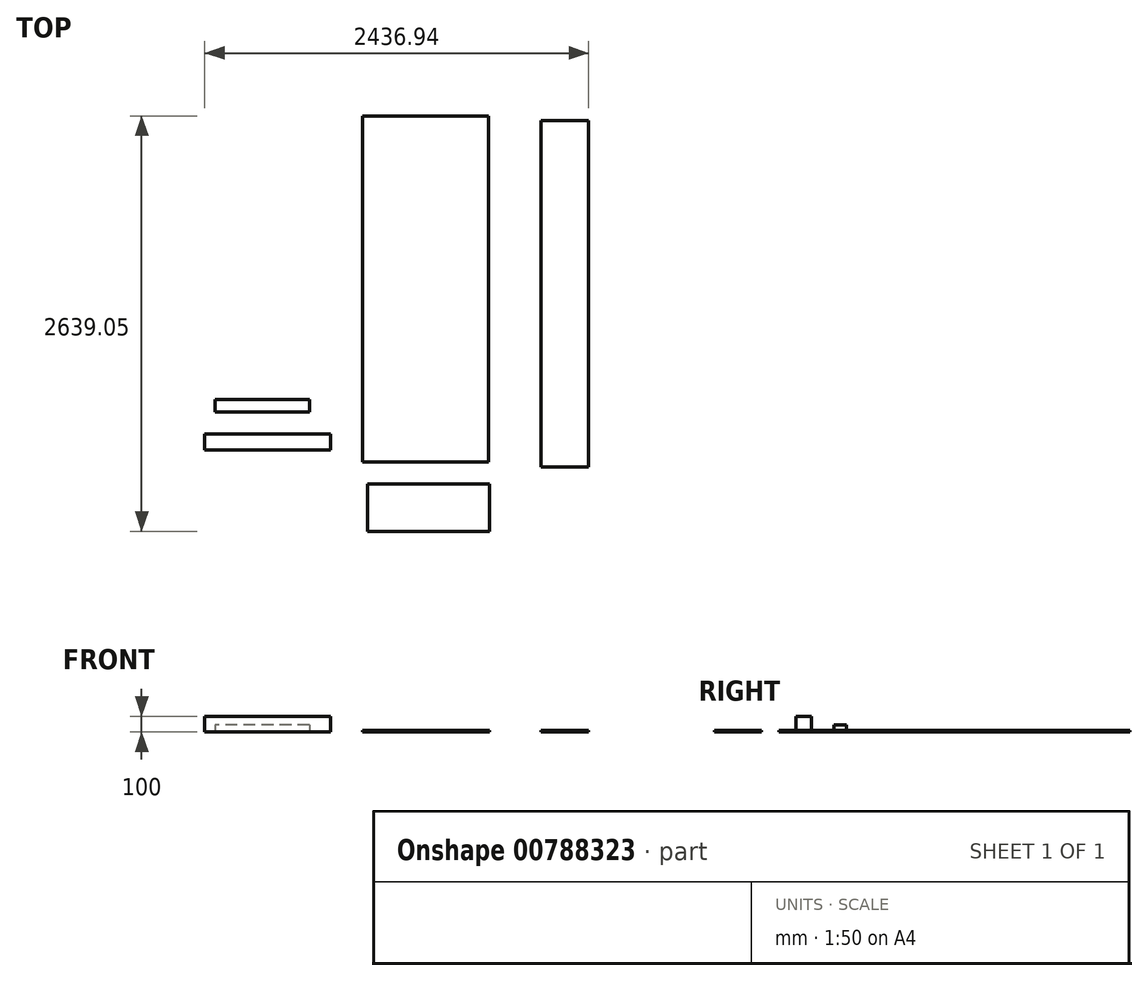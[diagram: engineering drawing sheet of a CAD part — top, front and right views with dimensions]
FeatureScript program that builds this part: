
annotation { "Feature Type Name" : "Feature", "Feature Type Description" : "" }
export const myFeature = defineFeature(function(context is Context, id is Id, definition is map)
    precondition{}
    {
        {
            var Q0;
            Q0=qCreatedBy(makeId("Top.planeOp"),FACE);
            var sketch = newSketch(context, id + "F0", { "sketchPlane" : qUnion([Q0])});
            skLineSegment(sketch, "E0.bottom", {"start": v(-918.13, 2121.97) * mm, "end": v(-118.13, 2121.97) * mm});
            skLineSegment(sketch, "E0.top", {"start": v(-918.13, -78.03) * mm, "end": v(-118.13, -78.03) * mm});
            skLineSegment(sketch, "E0.left", {"start": v(-918.13, 2121.97) * mm, "end": v(-918.13, -78.03) * mm});
            skLineSegment(sketch, "E0.right", {"start": v(-118.13, 2121.97) * mm, "end": v(-118.13, -78.03) * mm});
            skSolve(sketch);
        }
        {
            var Q0;
            Q0=qCreatedBy(makeId("Top.planeOp"),FACE);
            var sketch = newSketch(context, id + "F1", { "sketchPlane" : qUnion([Q0])});
            skLineSegment(sketch, "E1.bottom", {"start": v(216.24, -107.32) * mm, "end": v(516.24, -107.32) * mm});
            skLineSegment(sketch, "E1.top", {"start": v(216.24, 2092.68) * mm, "end": v(516.24, 2092.68) * mm});
            skLineSegment(sketch, "E1.left", {"start": v(216.24, -107.32) * mm, "end": v(216.24, 2092.68) * mm});
            skLineSegment(sketch, "E1.right", {"start": v(516.24, -107.32) * mm, "end": v(516.24, 2092.68) * mm});
            skSolve(sketch);
        }
        {
            var Q0;
            Q0=makeQuery(id+"F0.imprint","IMPRINT",FACE,{"disambiguationData":[TD([[makeQuery(id+"F0.imprint","IMPRINT",EDGE,{"derivedFrom":sQuery(id+"F0.wireOp",EDGE,"E0.bottom")}),-1.0]])]});
            extrude(context, id + "F2", {"entities" : qUnion([Q0]), "depth" : 12 * mm, "offsetDistance" : 25 * mm});
        }
        {
            var Q0;
            Q0 = qSketchRegion(id + "F1", true);
            extrude(context, id + "F3", {"entities" : qUnion([Q0]), "depth" : 12 * mm, "offsetDistance" : 25 * mm});
        }
        {
            var Q0;
            Q0=qCreatedBy(makeId("Top.planeOp"),FACE);
            var sketch = newSketch(context, id + "F4", { "sketchPlane" : qUnion([Q0])});
            skLineSegment(sketch, "E2.bottom", {"start": v(-887.62, -217.08) * mm, "end": v(-111.62, -217.08) * mm});
            skLineSegment(sketch, "E2.top", {"start": v(-887.62, -517.08) * mm, "end": v(-111.62, -517.08) * mm});
            skLineSegment(sketch, "E2.left", {"start": v(-887.62, -217.08) * mm, "end": v(-887.62, -517.08) * mm});
            skLineSegment(sketch, "E2.right", {"start": v(-111.62, -217.08) * mm, "end": v(-111.62, -517.08) * mm});
            skSolve(sketch);
        }
        {
            var Q0;
            Q0=makeQuery(id+"F4.imprint","IMPRINT",FACE,{"disambiguationData":[TD([[makeQuery(id+"F4.imprint","IMPRINT",EDGE,{"derivedFrom":sQuery(id+"F4.wireOp",EDGE,"E2.bottom")}),-1.0]])]});
            extrude(context, id + "F5", {"entities" : qUnion([Q0]), "depth" : 12 * mm, "offsetDistance" : 25 * mm});
        }
        {
            var Q0;
            Q0=qCreatedBy(makeId("Top.planeOp"),FACE);
            var sketch = newSketch(context, id + "F6", { "sketchPlane" : qUnion([Q0])});
            skLineSegment(sketch, "E3.bottom", {"start": v(-1120.7, 0) * mm, "end": v(-1920.7, 0) * mm});
            skLineSegment(sketch, "E3.top", {"start": v(-1120.7, 100) * mm, "end": v(-1920.7, 100) * mm});
            skLineSegment(sketch, "E3.left", {"start": v(-1120.7, 0) * mm, "end": v(-1120.7, 100) * mm});
            skLineSegment(sketch, "E3.right", {"start": v(-1920.7, 0) * mm, "end": v(-1920.7, 100) * mm});
            skSolve(sketch);
        }
        {
            var Q0;
            Q0=makeQuery(id+"F6.imprint","IMPRINT",FACE,{"disambiguationData":[TD([[makeQuery(id+"F6.imprint","IMPRINT",EDGE,{"derivedFrom":sQuery(id+"F6.wireOp",EDGE,"E3.bottom")}),-1.0]])]});
            extrude(context, id + "F7", {"entities" : qUnion([Q0]), "depth" : 100 * mm, "offsetDistance" : 25 * mm});
        }
        {
            var Q0;
            Q0=qCreatedBy(makeId("Top.planeOp"),FACE);
            var sketch = newSketch(context, id + "F8", { "sketchPlane" : qUnion([Q0])});
            skLineSegment(sketch, "E4.bottom", {"start": v(-1254.83, 241.2) * mm, "end": v(-1854.83, 241.2) * mm});
            skLineSegment(sketch, "E4.top", {"start": v(-1254.83, 321.2) * mm, "end": v(-1854.83, 321.2) * mm});
            skLineSegment(sketch, "E4.left", {"start": v(-1254.83, 241.2) * mm, "end": v(-1254.83, 321.2) * mm});
            skLineSegment(sketch, "E4.right", {"start": v(-1854.83, 241.2) * mm, "end": v(-1854.83, 321.2) * mm});
            skSolve(sketch);
        }
        {
            var Q0;
            Q0=makeQuery(id+"F8.imprint","IMPRINT",FACE,{"disambiguationData":[TD([[makeQuery(id+"F8.imprint","IMPRINT",EDGE,{"derivedFrom":sQuery(id+"F8.wireOp",EDGE,"E4.bottom")}),-1.0]])]});
            extrude(context, id + "F9", {"entities" : qUnion([Q0]), "depth" : 47 * mm, "offsetDistance" : 25 * mm});
        }
    });
